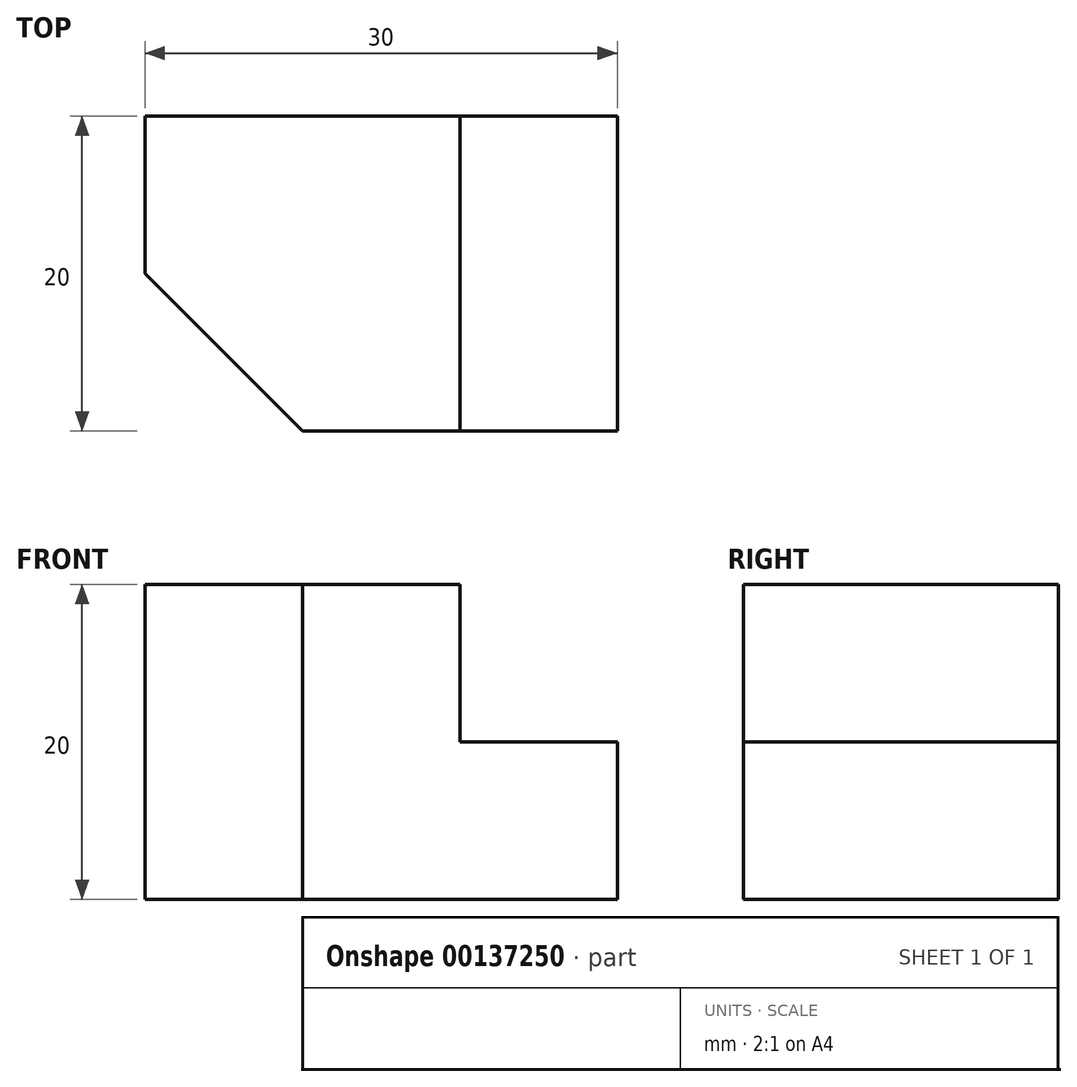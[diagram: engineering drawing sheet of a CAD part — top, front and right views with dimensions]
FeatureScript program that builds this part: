
annotation { "Feature Type Name" : "Feature", "Feature Type Description" : "" }
export const myFeature = defineFeature(function(context is Context, id is Id, definition is map)
    precondition{}
    {
        {
            var Q0;
            Q0=qCreatedBy(makeId("Top.planeOp"),FACE);
            var sketch = newSketch(context, id + "F0", { "sketchPlane" : qUnion([Q0])});
            skLineSegment(sketch, "E0", {"start": v(0, 0) * mm, "end": v(20, 0) * mm});
            skLineSegment(sketch, "E1", {"start": v(20, 0) * mm, "end": v(20, 20) * mm});
            skLineSegment(sketch, "E2", {"start": v(20, 20) * mm, "end": v(-10, 20) * mm});
            skLineSegment(sketch, "E3", {"start": v(-10, 20) * mm, "end": v(-10, 10) * mm});
            skLineSegment(sketch, "E4", {"start": v(-10, 10) * mm, "end": v(0, 0) * mm});
            skSolve(sketch);
        }
        {
            var Q0;
            Q0 = qSketchRegion(id + "F0", true);
            extrude(context, id + "F1", {"entities" : qUnion([Q0]), "depth" : 20 * mm});
        }
        {
            var Q0;
            Q0=makeQuery(id+"F1.opExtrude","CAP_FACE",FACE,{"disambiguationData":[OSD([sQuery(id+"F0.wireOp",EDGE,"E0"),sQuery(id+"F0.wireOp",EDGE,"E1"),sQuery(id+"F0.wireOp",EDGE,"E2"),sQuery(id+"F0.wireOp",EDGE,"E3"),sQuery(id+"F0.wireOp",EDGE,"E4")])],"isStart":false});
            var sketch = newSketch(context, id + "F2", { "sketchPlane" : qUnion([Q0])});
            skLineSegment(sketch, "E5.bottom", {"start": v(20, 20) * mm, "end": v(10, 20) * mm});
            skLineSegment(sketch, "E5.top", {"start": v(20, 0) * mm, "end": v(10, 0) * mm});
            skLineSegment(sketch, "E5.left", {"start": v(20, 20) * mm, "end": v(20, 0) * mm});
            skLineSegment(sketch, "E5.right", {"start": v(10, 20) * mm, "end": v(10, 0) * mm});
            skSolve(sketch);
        }
        {
            var Q0;
            Q0 = qSketchRegion(id + "F2", true);
            extrude(context, id + "F3", {"entities" : qUnion([Q0]), "operationType" : NewBodyOperationType.REMOVE, "oppositeDirection" : true, "depth" : 10 * mm});
        }
    });
